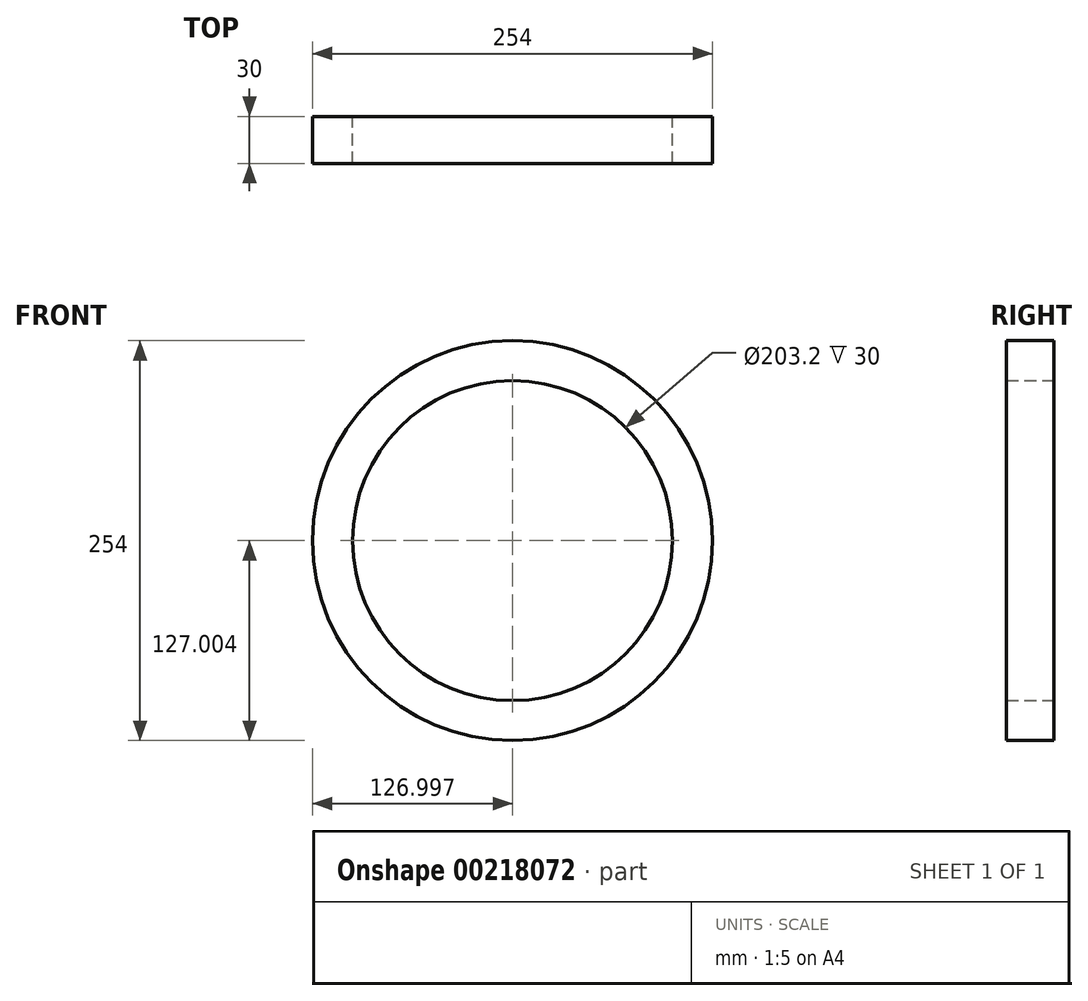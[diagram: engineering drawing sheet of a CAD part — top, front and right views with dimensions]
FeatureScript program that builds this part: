
annotation { "Feature Type Name" : "Feature", "Feature Type Description" : "" }
export const myFeature = defineFeature(function(context is Context, id is Id, definition is map)
    precondition{}
    {
        {
            var Q0;
            Q0=qCreatedBy(makeId("Front.planeOp"),FACE);
            var sketch = newSketch(context, id + "F0", { "sketchPlane" : qUnion([Q0])});
            skCircle(sketch, "E0", {"center": v(-18.1, 4.9) * mm, "radius": 101.6 * mm});
            skCircle(sketch, "E1", {"center": v(-18.1, 4.9) * mm, "radius": 127 * mm});
            skSolve(sketch);
        }
        {
            var Q0;
            Q0=makeQuery(id+"F0.imprint","IMPRINT",FACE,{"disambiguationData":[TD([[makeQuery(id+"F0.imprint","IMPRINT",EDGE,{"derivedFrom":sQuery(id+"F0.wireOp",EDGE,"E0")}),-1.0]])]});
            extrude(context, id + "F1", {"entities" : qUnion([Q0]), "depth" : 30 * mm});
        }
    });
